# Revit family: Lighting-CommercialSector-GEWISS-ELIA-CL-LED_CEILING_D300
name_source: partatom
category: Apparecchi per illuminazione
units: mm (PartAtom-declared; Revit-internal decimal feet)

## family parameters
Condiviso = No
Host = Superficie
Punto di calcolo locali = Sì
Quota connettore circolare = Usa diametro
Sorgente d'illuminazione = Sì
Taglio con vuoti quando caricato = No
Tipo di parte = Normale

## types (4) — shared parameters
Angolo inclinazione = -90.00°
Application = Indoor
Catalogue = LIGHTING
Catalogue Range = ELIA CL
Colour = White
Colour temperature = 4000K
Colour temperature: = 4000K
Emetti da lunghezza linea = 610 mm
FORO_CONTROSOFFITTO = 80 mm  [stored 0.262467 ft]
File diagramma fotometrico = GWF1316MA840.IES
Filtro dei colori = 16777215
IDF = a2752f49-e9ed-4fba-ae51-27c1a58457b9
IDT = a0104f8a-d9bd-4c2b-84a2-ea762e196079
IP degree = IP20 - IP54
Immagine tipo = ELIA_CL.jpg
Installation = Surface mounted
Insulation class = II
LARGHEZZA_FORO = 820 mm
LED = <Per categoria>
LED Life time (L80B50) = L80 B50 (Tq25°) = 50.000h
LUNGHEZZA FORO = 969 mm
L_lampada = 1500 mm
Lamp = LED
Lumen output (lm) = 2550
Optic = Diffusing opal
POSIZIONE = 80000
Produttore = GEWISS S.p.A.
Prospetto di default = 1219 mm
SEO = Surface mounted
STRUTTURA = <Per categoria>
Shock resistance = IK08
System power = 25W
Technical sheet = https://www.gewiss.com
Type of lamp = LED
Type of light source = LED - Not replaceable
Typology = Surface mounted
URL = https://www.gewiss.com
Variazione temperatura colore lampada con luminosità attenuata = <Nessuno>
Version file RFA = 20.0
Voltage = 220-240 VÂ
Warranty = 5 years

## per-type parameters (varying)
| type | Descrizione | Dimensions (mm) | Modello | Operating temperature: | Weight (kg) | Weight (kg): | Working temperature |
| GWF1315MA840 - ELIA CL M2 OPAL DIFF 40K ST.ALONE MW | ELIA CL M2 OPAL DIFF 40K ST.ALONE MW | With sensor / Emergency | GWF1315MA840 | -20° +45° | 0,8 | 0,8 | -20° +45° |
| GWF1310MA840 - ELIA CL M2 OPAL DIFF 40K ST.ALONE ONOFF | ELIA CL M2 OPAL DIFF 40K ST.ALONE ONOFF | Standard | GWF1310MA840 | -20° +45° | 0,5 | 0,5 | -20° +45° |
| GWF1316MA840 - ELIA CL M2 OPAL DIFF 40K ST.ALONE MW EM | ELIA CL M2 OPAL DIFF 40K ST.ALONE MW EM | With sensor / Emergency | GWF1316MA840 | -0° +45° | 0,9 | 0,9 | -0° +45° |
| GWF1314MA840 - ELIA CL M2 OPAL DIFF 40K ST.ALONE EM | ELIA CL M2 OPAL DIFF 40K ST.ALONE EM | With sensor / Emergency | GWF1314MA840 | -0° +45° | 0,8 | 0,8 | -0° +45° |

note: [stored X ft] marks values corroborated as IEEE doubles in the binary element streams (Revit-internal decimal feet)
